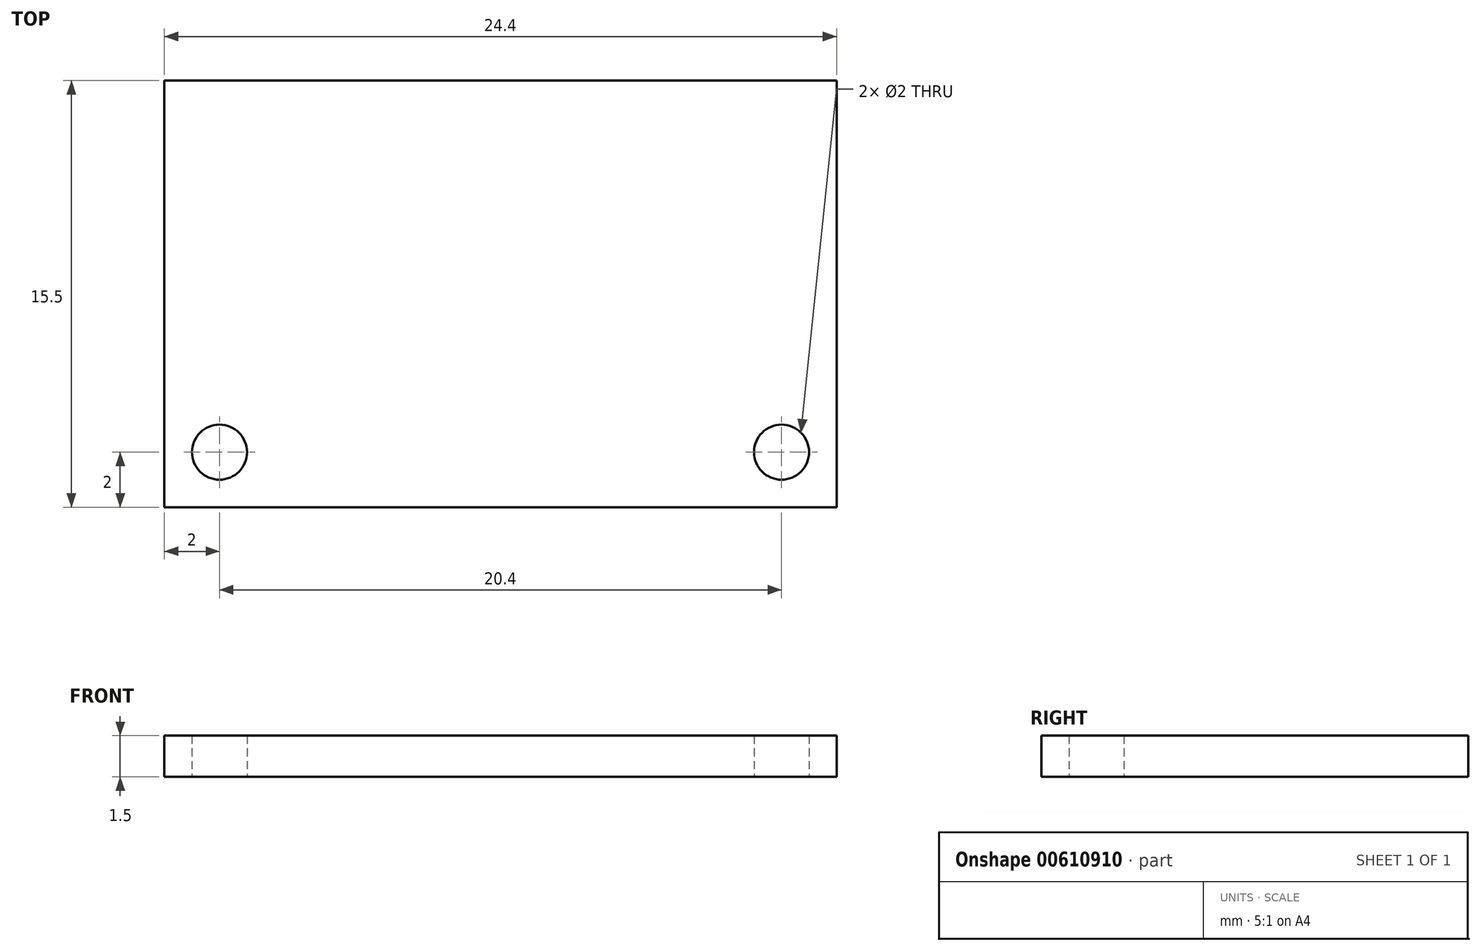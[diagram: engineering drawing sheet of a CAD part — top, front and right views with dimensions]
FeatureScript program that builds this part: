
annotation { "Feature Type Name" : "Feature", "Feature Type Description" : "" }
export const myFeature = defineFeature(function(context is Context, id is Id, definition is map)
    precondition{}
    {
        {
            var Q0;
            Q0=qCreatedBy(makeId("Top.planeOp"),FACE);
            var sketch = newSketch(context, id + "F0", { "sketchPlane" : qUnion([Q0])});
            skLineSegment(sketch, "E0.bottom", {"start": v(12.2, -7.75) * mm, "end": v(-12.2, -7.75) * mm});
            skLineSegment(sketch, "E0.top", {"start": v(12.2, 7.75) * mm, "end": v(-12.2, 7.75) * mm});
            skLineSegment(sketch, "E0.left", {"start": v(12.2, -7.75) * mm, "end": v(12.2, 7.75) * mm});
            skLineSegment(sketch, "E0.right", {"start": v(-12.2, -7.75) * mm, "end": v(-12.2, 7.75) * mm});
            skPoint(sketch, "E0.middle", {"position": v(0, 0) * mm});
            skCircle(sketch, "E1", {"center": v(10.2, -5.75) * mm, "radius": 1 * mm});
            skCircle(sketch, "E2.MirrorC", {"center": v(-10.2, -5.75) * mm, "radius": 1 * mm});
            skSolve(sketch);
        }
        {
            var Q0;
            Q0 = qSketchRegion(id + "F0", true);
            extrude(context, id + "F1", {"entities" : qUnion([Q0]), "depth" : 1.5 * mm, "offsetDistance" : 25 * mm});
        }
    });
